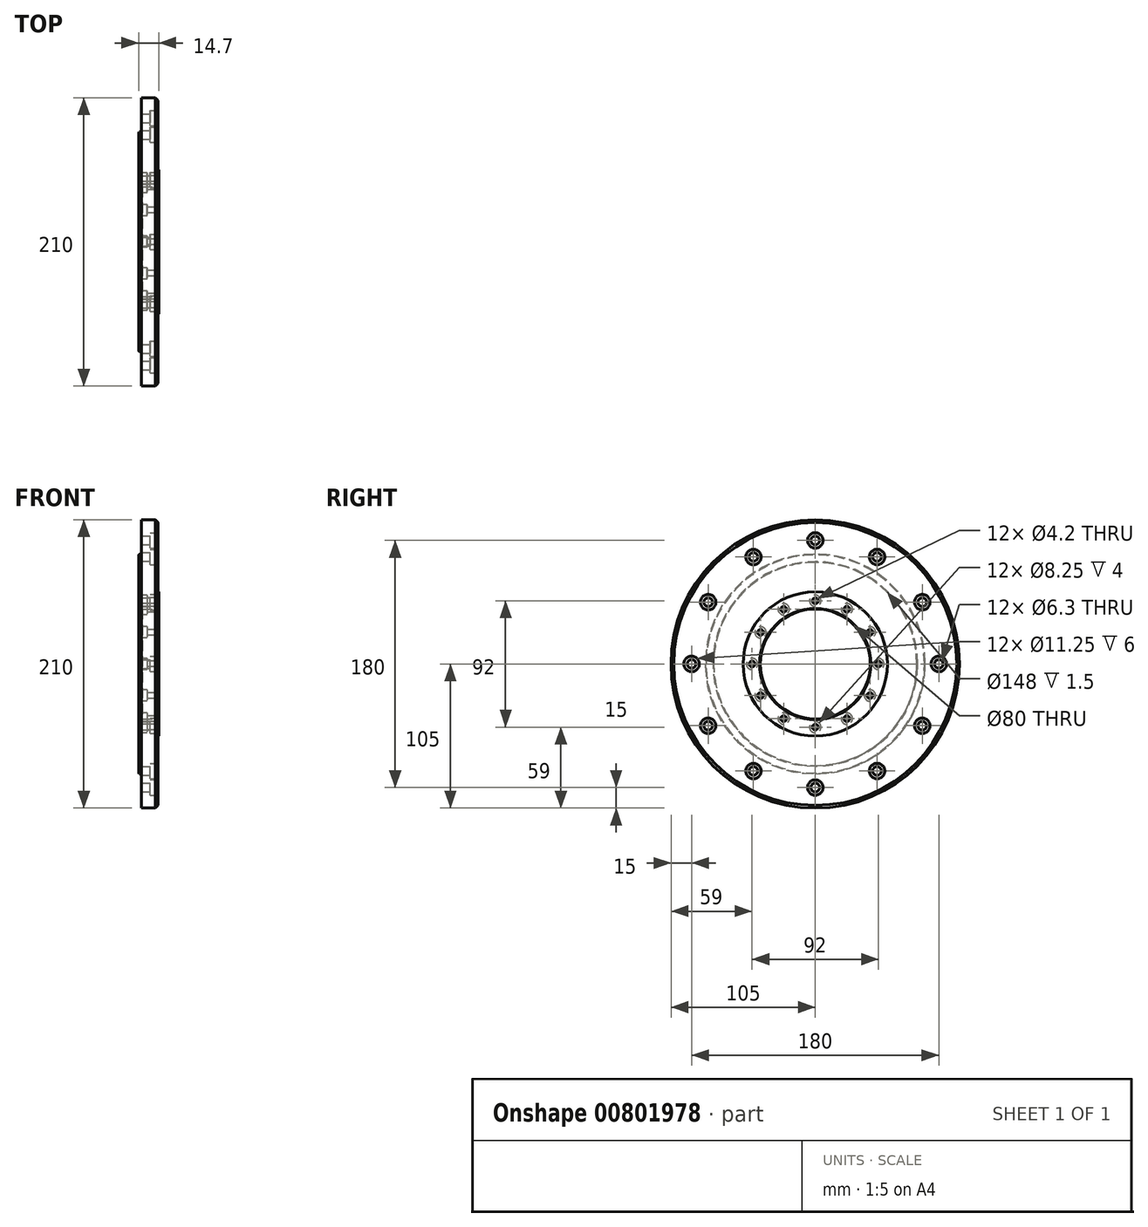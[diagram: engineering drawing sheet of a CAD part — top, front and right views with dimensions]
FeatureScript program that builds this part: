
annotation { "Feature Type Name" : "Feature", "Feature Type Description" : "" }
export const myFeature = defineFeature(function(context is Context, id is Id, definition is map)
    precondition{}
    {
        {
            var Q0;
            Q0=qCreatedBy(makeId("Front.planeOp"),FACE);
            var sketch = newSketch(context, id + "F0", { "sketchPlane" : qUnion([Q0])});
            skLineSegment(sketch, "E0", {"start": v(91.08, 0) * mm, "end": v(-135.26, 0) * mm, "construction": true});
            skLineSegment(sketch, "E1", {"start": v(-4.62, 80) * mm, "end": v(-4.62, 105) * mm});
            skLineSegment(sketch, "E2", {"start": v(-4.62, 105) * mm, "end": v(7.58, 105) * mm});
            skLineSegment(sketch, "E3", {"start": v(7.58, 105) * mm, "end": v(7.58, 52.5) * mm});
            skLineSegment(sketch, "E4", {"start": v(7.58, 52.5) * mm, "end": v(8.08, 52.5) * mm});
            skLineSegment(sketch, "E5", {"start": v(8.08, 52.5) * mm, "end": v(8.08, 40) * mm});
            skLineSegment(sketch, "E6", {"start": v(-4.62, 80) * mm, "end": v(-6.62, 80) * mm});
            skLineSegment(sketch, "E7", {"start": v(8.08, 40) * mm, "end": v(-4.62, 40) * mm});
            skLineSegment(sketch, "E8", {"start": v(-6.62, 80) * mm, "end": v(-6.62, 74) * mm});
            skLineSegment(sketch, "E9", {"start": v(-6.62, 74) * mm, "end": v(-4.62, 74) * mm});
            skLineSegment(sketch, "E10", {"start": v(-4.62, 74) * mm, "end": v(-4.62, 40) * mm});
            skPoint(sketch, "E11.orphan", {"position": v(-6.62, 40) * mm});
            skSolve(sketch);
        }
        {
            var Q0;
            Q0=qSketchRegion(id+"F0",true);
            var Q1;
            Q1=sQuery(id+"F0.wireOp",EDGE,"E0");
            revolve(context, id + "F1", {"entities" : qUnion([Q0]), "axis" : qUnion([Q1]), "revolveType" : RevolveType.FULL});
        }
        {
            var Q0;
            Q0=makeQuery(id+"F1.opRevolve","SWEPT_FACE",FACE,{"disambiguationData":[OSD([sQuery(id+"F0.wireOp",EDGE,"E1")])]});
            var sketch = newSketch(context, id + "F2", { "sketchPlane" : qUnion([Q0])});
            skPoint(sketch, "E12", {"position": v(0, 0) * mm});
            skPoint(sketch, "E13", {"position": v(0, 46) * mm});
            skPoint(sketch, "E14", {"position": v(23, 39.84) * mm});
            skPoint(sketch, "E15", {"position": v(39.84, 23) * mm});
            skPoint(sketch, "E16", {"position": v(46, 0) * mm});
            skPoint(sketch, "E17", {"position": v(39.84, -23) * mm});
            skPoint(sketch, "E18", {"position": v(23, -39.84) * mm});
            skPoint(sketch, "E19", {"position": v(0, -46) * mm});
            skPoint(sketch, "E20", {"position": v(-23, -39.84) * mm});
            skPoint(sketch, "E21", {"position": v(-39.84, -23) * mm});
            skPoint(sketch, "E22", {"position": v(-46, 0) * mm});
            skPoint(sketch, "E23", {"position": v(-39.84, 23) * mm});
            skPoint(sketch, "E24", {"position": v(-23, 39.84) * mm});
            skSolve(sketch);
        }
        {
            var Q0;
            Q0=makeQuery(id+"F1.opRevolve","SWEPT_FACE",FACE,{"disambiguationData":[OSD([sQuery(id+"F0.wireOp",EDGE,"E3")])]});
            var sketch = newSketch(context, id + "F3", { "sketchPlane" : qUnion([Q0])});
            skPoint(sketch, "E25.center", {"position": v(0, 0) * mm});
            skPoint(sketch, "E26", {"position": v(0, 90) * mm});
            skPoint(sketch, "E27", {"position": v(45, 77.94) * mm});
            skPoint(sketch, "E28", {"position": v(77.94, 45) * mm});
            skPoint(sketch, "E29", {"position": v(90, 0) * mm});
            skPoint(sketch, "E30", {"position": v(77.94, -45) * mm});
            skPoint(sketch, "E31", {"position": v(45, -77.94) * mm});
            skPoint(sketch, "E32", {"position": v(0, -90) * mm});
            skPoint(sketch, "E33", {"position": v(-45, -77.94) * mm});
            skPoint(sketch, "E34", {"position": v(-77.94, -45) * mm});
            skPoint(sketch, "E35", {"position": v(-90, 0) * mm});
            skPoint(sketch, "E36", {"position": v(-77.94, 45) * mm});
            skPoint(sketch, "E37", {"position": v(-45, 77.94) * mm});
            skSolve(sketch);
        }
        {
            var Q0;
            Q0=sQuery(id+"F2.wireOp",VERTEX,"E13");
            var Q1;
            Q1=sQuery(id+"F2.wireOp",VERTEX,"E14");
            var Q2;
            Q2=sQuery(id+"F2.wireOp",VERTEX,"E15");
            var Q3;
            Q3=sQuery(id+"F2.wireOp",VERTEX,"E16");
            var Q4;
            Q4=sQuery(id+"F2.wireOp",VERTEX,"E17");
            var Q5;
            Q5=sQuery(id+"F2.wireOp",VERTEX,"E18");
            var Q6;
            Q6=sQuery(id+"F2.wireOp",VERTEX,"E19");
            var Q7;
            Q7=sQuery(id+"F2.wireOp",VERTEX,"E20");
            var Q8;
            Q8=sQuery(id+"F2.wireOp",VERTEX,"E22");
            var Q9;
            Q9=sQuery(id+"F2.wireOp",VERTEX,"E21");
            var Q10;
            Q10=sQuery(id+"F2.wireOp",VERTEX,"E23");
            var Q11;
            Q11=sQuery(id+"F2.wireOp",VERTEX,"E24");
            var Q12;
            Q12=makeQuery(id+"F1.opRevolve","SWEPT_BODY",BODY,{"disambiguationData":[OSD([sQuery(id+"F0.wireOp",EDGE,"8f36247e-526f-4479-acc4-7eec241f1e58"),sQuery(id+"F0.wireOp",EDGE,"E1"),sQuery(id+"F0.wireOp",EDGE,"E2"),sQuery(id+"F0.wireOp",EDGE,"E3"),sQuery(id+"F0.wireOp",EDGE,"E4"),sQuery(id+"F0.wireOp",EDGE,"E5")])]});
            hole(context, id + "F4", {"style" : HoleStyle.C_BORE, "endStyle" : HoleEndStyle.THROUGH, "standardTappedOrClearance" : lookupTablePath({ "standard" : "ISO", "fit" : "Close", "size" : "M4", "type" : "Clearance" }), "standardBlindInLast" : lookupTablePath({ "fit" : "Close", "standard" : "ISO", "size" : "M4", "type" : "Clearance" }), "holeDiameter" : 4.2 * mm, "cBoreDiameter" : 8.25 * mm, "cBoreDepth" : 4 * mm, "tappedDepth" : 16.82 * mm, "tapClearance" : 3, "startFromSketch" : true, "locations" : qUnion([Q0, Q1, Q2, Q3, Q4, Q5, Q6, Q7, Q8, Q9, Q10, Q11]), "scope" : qUnion([Q12])});
        }
        {
            var Q0;
            Q0=sQuery(id+"F3.wireOp",VERTEX,"E26");
            var Q1;
            Q1=sQuery(id+"F3.wireOp",VERTEX,"E27");
            var Q2;
            Q2=sQuery(id+"F3.wireOp",VERTEX,"E28");
            var Q3;
            Q3=sQuery(id+"F3.wireOp",VERTEX,"E29");
            var Q4;
            Q4=sQuery(id+"F3.wireOp",VERTEX,"E30");
            var Q5;
            Q5=sQuery(id+"F3.wireOp",VERTEX,"E31");
            var Q6;
            Q6=sQuery(id+"F3.wireOp",VERTEX,"E32");
            var Q7;
            Q7=sQuery(id+"F3.wireOp",VERTEX,"E33");
            var Q8;
            Q8=sQuery(id+"F3.wireOp",VERTEX,"E34");
            var Q9;
            Q9=sQuery(id+"F3.wireOp",VERTEX,"E35");
            var Q10;
            Q10=sQuery(id+"F3.wireOp",VERTEX,"E36");
            var Q11;
            Q11=sQuery(id+"F3.wireOp",VERTEX,"E37");
            var Q12;
            Q12=makeQuery(id+"F1.opRevolve","SWEPT_BODY",BODY,{"disambiguationData":[OSD([sQuery(id+"F0.wireOp",EDGE,"8f36247e-526f-4479-acc4-7eec241f1e58"),sQuery(id+"F0.wireOp",EDGE,"E1"),sQuery(id+"F0.wireOp",EDGE,"E2"),sQuery(id+"F0.wireOp",EDGE,"E3"),sQuery(id+"F0.wireOp",EDGE,"E4"),sQuery(id+"F0.wireOp",EDGE,"E5")])]});
            hole(context, id + "F5", {"style" : HoleStyle.C_BORE, "endStyle" : HoleEndStyle.THROUGH, "standardTappedOrClearance" : lookupTablePath({ "standard" : "ISO", "fit" : "Close", "size" : "M6", "type" : "Clearance" }), "standardBlindInLast" : lookupTablePath({ "fit" : "Close", "standard" : "ISO", "size" : "M6", "type" : "Clearance" }), "holeDiameter" : 6.3 * mm, "cBoreDiameter" : 11.25 * mm, "cBoreDepth" : 6 * mm, "tappedDepth" : 16.82 * mm, "tapClearance" : 3, "startFromSketch" : true, "locations" : qUnion([Q0, Q1, Q2, Q3, Q4, Q5, Q6, Q7, Q8, Q9, Q10, Q11]), "scope" : qUnion([Q12])});
        }
        {
            var Q0;
            Q0=makeQuery(id+"F1.opRevolve","SWEPT_EDGE",EDGE,{"disambiguationData":[OSD([sQuery(id+"F0.wireOp",EDGE,"E2"),sQuery(id+"F0.wireOp",EDGE,"E3")])]});
            chamfer(context, id + "F6", {"entities" : qUnion([Q0]), "width" : 2 * mm, "tangentPropagation" : true});
        }
        {
            var Q0;
            Q0=makeQuery(id+"F1.opRevolve","SWEPT_EDGE",EDGE,{"disambiguationData":[OSD([sQuery(id+"F0.wireOp",EDGE,"E6"),sQuery(id+"F0.wireOp",EDGE,"E8")])]});
            var Q1;
            Q1=makeQuery(id+"F1.opRevolve","SWEPT_EDGE",EDGE,{"disambiguationData":[OSD([sQuery(id+"F0.wireOp",EDGE,"E7"),sQuery(id+"F0.wireOp",EDGE,"E8")])]});
            chamfer(context, id + "F7", {"entities" : qUnion([Q0, Q1]), "width" : .5 * mm, "tangentPropagation" : true});
        }
    });
